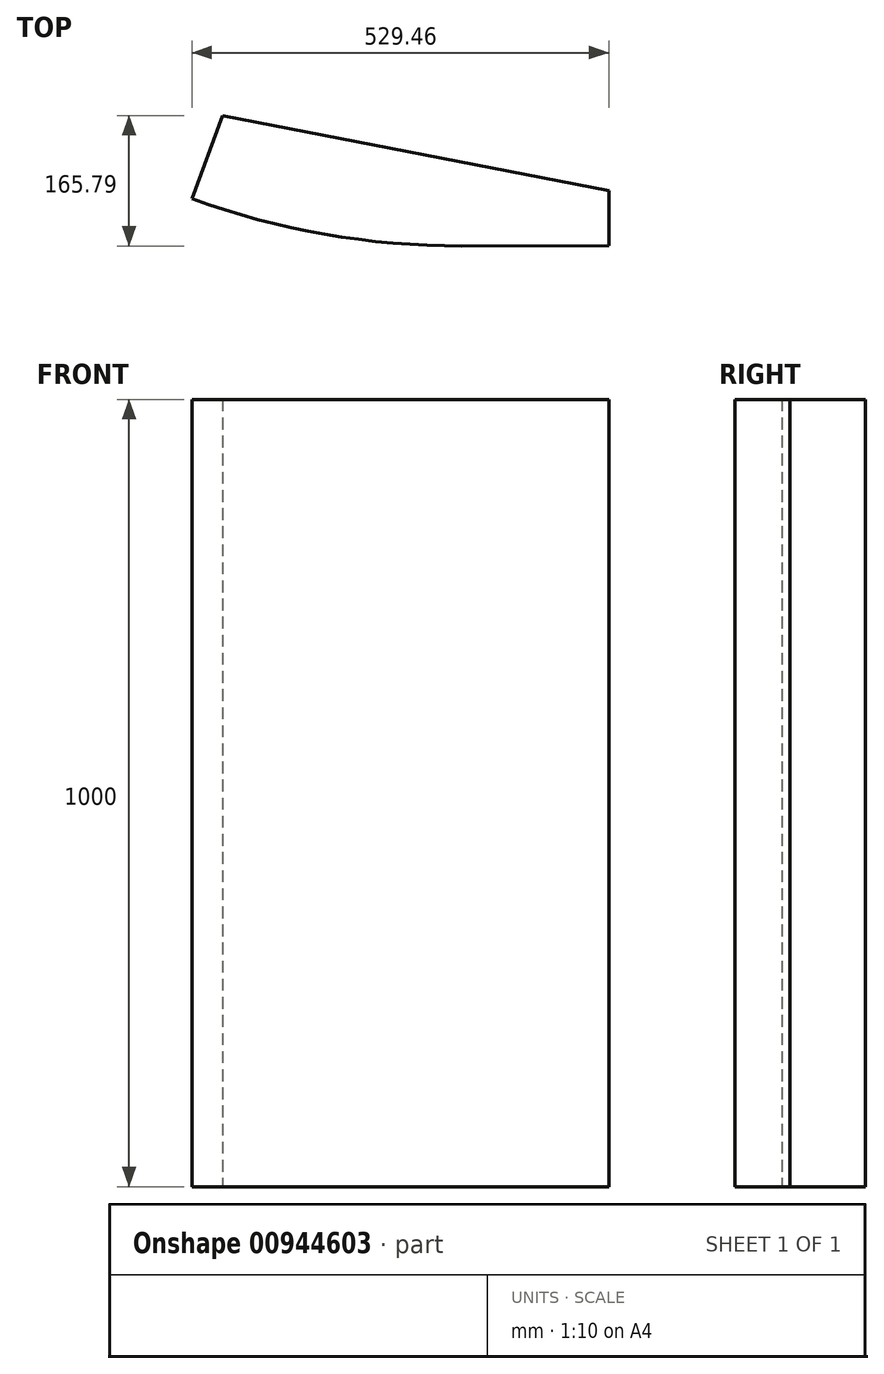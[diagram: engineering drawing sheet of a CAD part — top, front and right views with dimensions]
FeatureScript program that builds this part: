
annotation { "Feature Type Name" : "Feature", "Feature Type Description" : "" }
export const myFeature = defineFeature(function(context is Context, id is Id, definition is map)
    precondition{}
    {
        {
            var Q0;
            Q0=qCreatedBy(makeId("Top.planeOp"),FACE);
            var sketch = newSketch(context, id + "F0", { "sketchPlane" : qUnion([Q0])});
            skLineSegment(sketch, "E0", {"start": v(0, 0) * mm, "end": v(-115.87, 178.12) * mm});
            skLineSegment(sketch, "E1", {"start": v(-115.87, 178.12) * mm, "end": v(-195.87, 178.12) * mm});
            skLineSegment(sketch, "E2", {"start": v(-195.87, 178.12) * mm, "end": v(-195.87, 118.12) * mm});
            skLineSegment(sketch, "E3", {"start": v(-195.87, 118.12) * mm, "end": v(-183.87, 118.12) * mm});
            skLineSegment(sketch, "E4", {"start": v(0, 0) * mm, "end": v(-38.4, -105.84) * mm});
            skLineSegment(sketch, "E5", {"start": v(-183.87, 118.12) * mm, "end": v(-135.87, 118.12) * mm, "construction": true});
            skArc(sketch, "E6", {"start": v(-183.87, 118.12) * mm, "mid": v(-169.82, 84.18) * mm, "end": v(-135.87, 70.12) * mm});
            skLineSegment(sketch, "E7", {"start": v(-135.87, 70.12) * mm, "end": v(-135.87, 58.12) * mm});
            skLineSegment(sketch, "E8", {"start": v(-135.87, 58.12) * mm, "end": v(-123.87, 58.12) * mm});
            skLineSegment(sketch, "E9", {"start": v(-123.87, 58.12) * mm, "end": v(76.13, 58.12) * mm, "construction": true});
            skArc(sketch, "E10", {"start": v(-123.87, 58.12) * mm, "mid": v(-101.22, -34.33) * mm, "end": v(-38.4, -105.84) * mm});
            skLineSegment(sketch, "E11", {"start": v(76.13, 58.12) * mm, "end": v(7.92, -129.89) * mm, "construction": true});
            skLineSegment(sketch, "E12", {"start": v(-38.4, -105.84) * mm, "end": v(302.64, 834.2) * mm, "construction": true});
            skArc(sketch, "E13", {"start": v(-38.4, -105.84) * mm, "mid": v(130.1, -150.8) * mm, "end": v(303.86, -165.79) * mm});
            skLineSegment(sketch, "E14", {"start": v(302.64, 834.2) * mm, "end": v(303.86, -165.79) * mm, "construction": true});
            skLineSegment(sketch, "E15", {"start": v(303.86, -165.79) * mm, "end": v(491.06, -165.56) * mm});
            skLineSegment(sketch, "E16", {"start": v(491.06, -165.56) * mm, "end": v(490.97, -95.56) * mm});
            skLineSegment(sketch, "E17", {"start": v(490.97, -95.56) * mm, "end": v(0, 0) * mm});
            skSolve(sketch);
        }
        {
            var Q0;
            Q0=qCreatedBy(makeId("Front.planeOp"),FACE);
            var Q1;
            Q1=sQuery(id+"F0.wireOp",VERTEX,"E4.end");
            cPlane(context, id + "F1", {"entities" : qUnion([Q0, Q1]), "cplaneType" : CPlaneType.PLANE_POINT, "offset" : 104 * mm, "width" : 150 * mm, "height" : 150 * mm});
        }
        {
            var Q0;
            Q0=makeQuery(id+"F0.imprint","IMPRINT",FACE,{"disambiguationData":[TD([[makeQuery(id+"F0.imprint","IMPRINT",EDGE,{"derivedFrom":sQuery(id+"F0.wireOp",EDGE,"E4")}),1.0]])]});
            var sketch = newSketch(context, id + "F2", { "sketchPlane" : qUnion([Q0])});
            skLineSegment(sketch, "E18.0.0", {"start": v(491.06, -165.56) * mm, "end": v(490.97, -95.56) * mm});
            skLineSegment(sketch, "E18.0.1", {"start": v(490.97, -95.56) * mm, "end": v(0, 0) * mm});
            skLineSegment(sketch, "E18.0.2", {"start": v(0, 0) * mm, "end": v(-38.4, -105.84) * mm});
            skArc(sketch, "E18.0.3", {"start": v(-38.4, -105.84) * mm, "mid": v(130.1, -150.8) * mm, "end": v(303.86, -165.79) * mm});
            skLineSegment(sketch, "E18.0.4", {"start": v(303.86, -165.79) * mm, "end": v(491.06, -165.56) * mm});
            skSolve(sketch);
        }
        {
            var Q0;
            Q0=makeQuery(id+"F2.imprint","IMPRINT",FACE,{"disambiguationData":[TD([[makeQuery(id+"F2.imprint","IMPRINT",EDGE,{"derivedFrom":sQuery(id+"F2.wireOp",EDGE,"E18.0.0")}),1.0]])]});
            extrude(context, id + "F3", {"entities" : qUnion([Q0]), "depth" : 1000 * mm, "offsetDistance" : 25 * mm});
        }
    });
